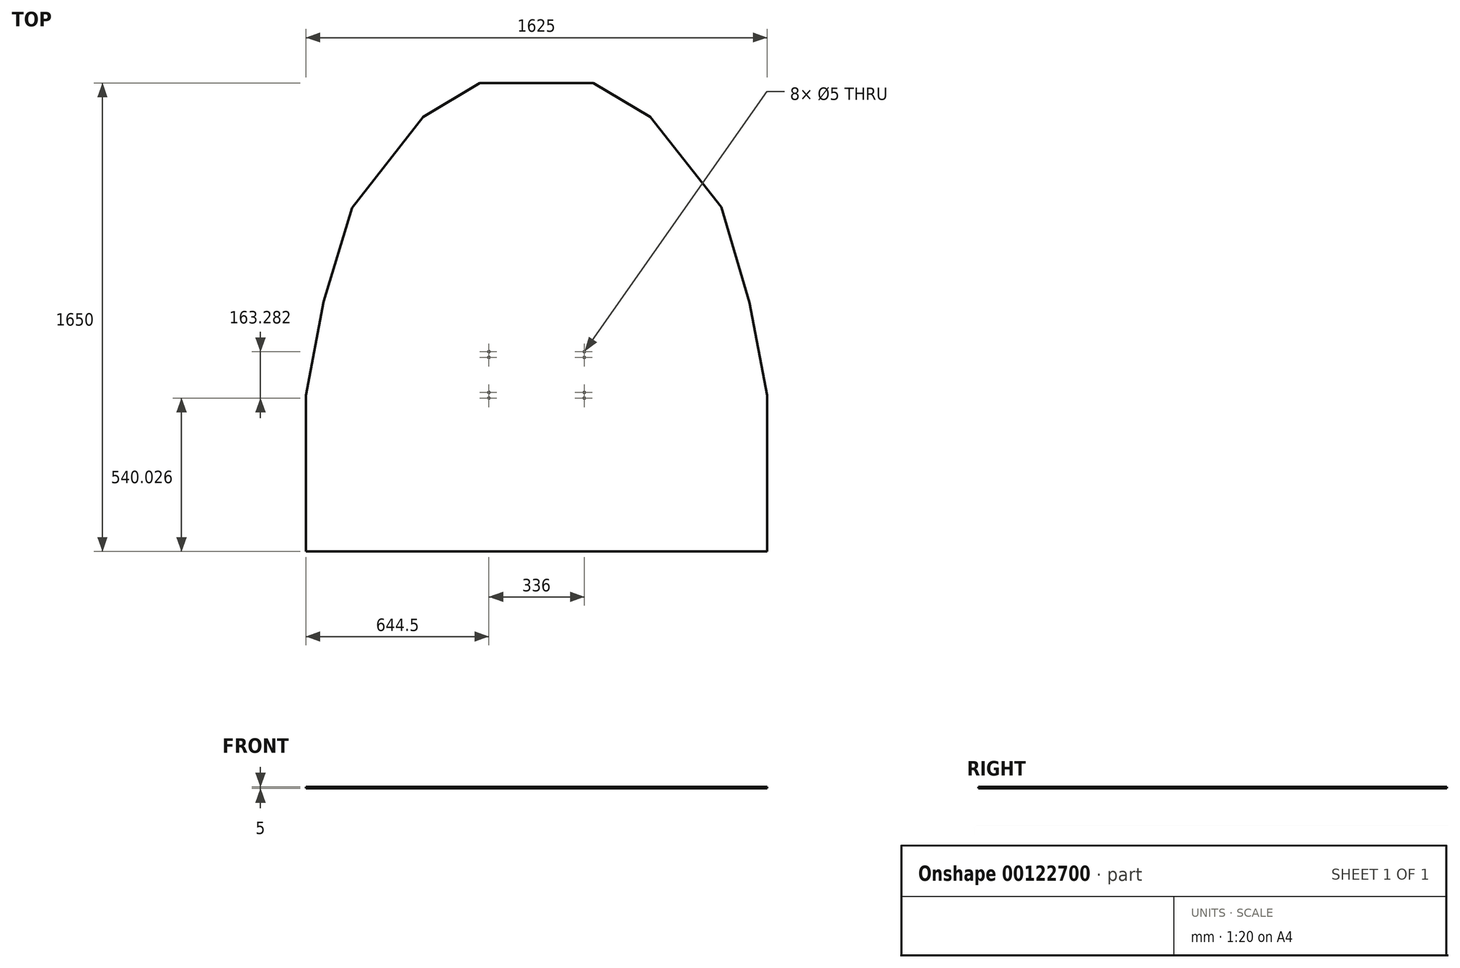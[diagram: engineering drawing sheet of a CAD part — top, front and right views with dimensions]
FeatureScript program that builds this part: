
annotation { "Feature Type Name" : "Feature", "Feature Type Description" : "" }
export const myFeature = defineFeature(function(context is Context, id is Id, definition is map)
    precondition{}
    {
        {
            var Q0;
            Q0=qCreatedBy(makeId("Top.planeOp"),FACE);
            var sketch = newSketch(context, id + "F0", { "sketchPlane" : qUnion([Q0])});
            skLineSegment(sketch, "E0.bottom", {"start": v(-812.5, -277.75) * mm, "end": v(812.5, -277.75) * mm});
            skLineSegment(sketch, "E0.top", {"start": v(-812.5, -827.75) * mm, "end": v(812.5, -827.75) * mm});
            skLineSegment(sketch, "E0.left", {"start": v(-812.5, -277.75) * mm, "end": v(-812.5, -827.75) * mm});
            skLineSegment(sketch, "E0.right", {"start": v(812.5, -277.75) * mm, "end": v(812.5, -827.75) * mm});
            skLineSegment(sketch, "E1", {"start": v(-812.5, -277.75) * mm, "end": v(-750, 52.25) * mm});
            skLineSegment(sketch, "E2", {"start": v(-750, 52.25) * mm, "end": v(750, 47.94) * mm});
            skLineSegment(sketch, "E3", {"start": v(750, 47.94) * mm, "end": v(812.5, -277.75) * mm});
            skLineSegment(sketch, "E4", {"start": v(-750, 52.25) * mm, "end": v(-650, 382.25) * mm});
            skLineSegment(sketch, "E5", {"start": v(-650, 382.25) * mm, "end": v(650, 384.5) * mm});
            skLineSegment(sketch, "E6", {"start": v(650, 384.5) * mm, "end": v(750, 47.94) * mm});
            skLineSegment(sketch, "E7", {"start": v(-650, 382.25) * mm, "end": v(-400, 702.25) * mm});
            skLineSegment(sketch, "E8", {"start": v(-400, 702.25) * mm, "end": v(400, 702.25) * mm});
            skLineSegment(sketch, "E9", {"start": v(400, 702.25) * mm, "end": v(650, 384.5) * mm});
            skLineSegment(sketch, "E10", {"start": v(0, 218.8) * mm, "end": v(0, -2047.11) * mm, "construction": true});
            skLineSegment(sketch, "E11", {"start": v(-400, 702.25) * mm, "end": v(-200, 822.25) * mm});
            skLineSegment(sketch, "E12", {"start": v(-200, 822.25) * mm, "end": v(200, 822.2) * mm});
            skLineSegment(sketch, "E13", {"start": v(200, 822.2) * mm, "end": v(400, 702.25) * mm});
            skCircle(sketch, "E14", {"center": v(168, -144.44) * mm, "radius": 2.5 * mm});
            skCircle(sketch, "E15", {"center": v(168, -124.44) * mm, "radius": 2.5 * mm});
            skCircle(sketch, "E16", {"center": v(168, -267.72) * mm, "radius": 2.5 * mm});
            skCircle(sketch, "E17", {"center": v(168, -287.72) * mm, "radius": 2.5 * mm});
            skCircle(sketch, "E18.MirrorC", {"center": v(-168, -287.72) * mm, "radius": 2.5 * mm});
            skCircle(sketch, "E19.MirrorC", {"center": v(-168, -267.72) * mm, "radius": 2.5 * mm});
            skCircle(sketch, "E20.MirrorC", {"center": v(-168, -144.44) * mm, "radius": 2.5 * mm});
            skCircle(sketch, "E21.MirrorC", {"center": v(-168, -124.44) * mm, "radius": 2.5 * mm});
            skSolve(sketch);
        }
        {
            var Q0;
            Q0=qSketchRegion(id+"F0",true);
            extrude(context, id + "F1", {"entities" : qUnion([Q0]), "oppositeDirection" : true, "depth" : 5 * mm});
        }
    });
